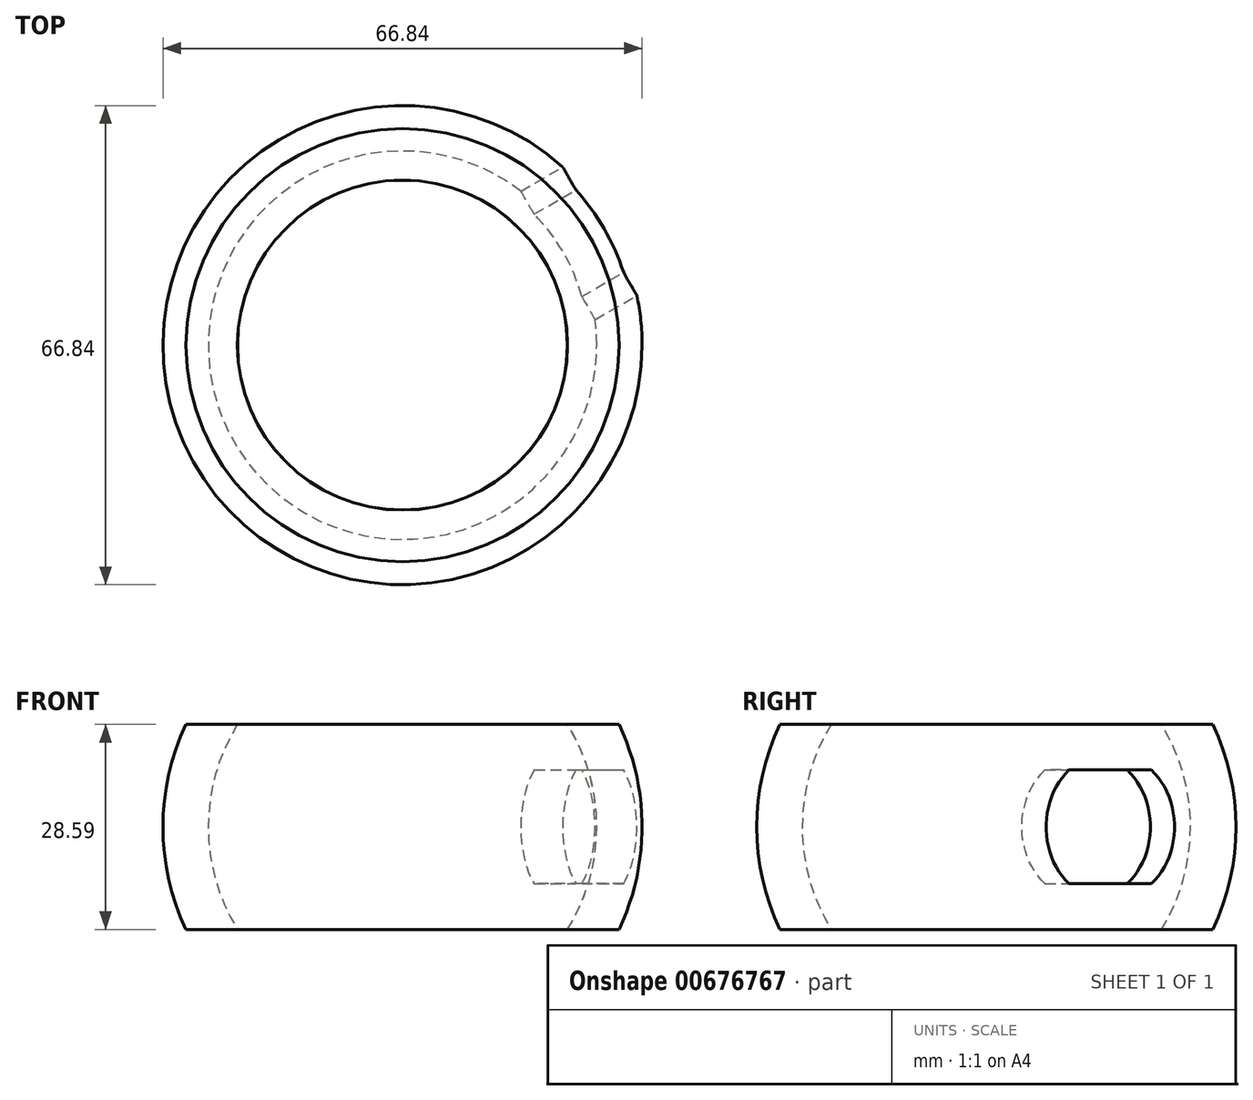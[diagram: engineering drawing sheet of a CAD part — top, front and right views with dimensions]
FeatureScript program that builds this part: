
annotation { "Feature Type Name" : "Feature", "Feature Type Description" : "" }
export const myFeature = defineFeature(function(context is Context, id is Id, definition is map)
    precondition{}
    {
        {
            var Q0;
            Q0=qCreatedBy(makeId("Front.planeOp"),FACE);
            var sketch = newSketch(context, id + "F0", { "sketchPlane" : qUnion([Q0])});
            skArc(sketch, "E0", {"start": v(-23.02, 0) * mm, "mid": v(-27.1, -14.3) * mm, "end": v(-23.01, -28.59) * mm});
            skLineSegment(sketch, "E1", {"start": v(-23.01, -28.59) * mm, "end": v(-30.2, -28.59) * mm});
            skArc(sketch, "E2", {"start": v(-30.21, 0) * mm, "mid": v(-33.42, -14.3) * mm, "end": v(-30.2, -28.59) * mm});
            skLineSegment(sketch, "E3", {"start": v(-23.02, 0) * mm, "end": v(-30.21, 0) * mm});
            skLineSegment(sketch, "E4", {"start": v(0, 0) * mm, "end": v(0, -26.06) * mm});
            skSolve(sketch);
        }
        {
            var Q0;
            Q0=makeQuery(id+"F0.imprint","IMPRINT",FACE,{"disambiguationData":[TD([[makeQuery(id+"F0.imprint","IMPRINT",EDGE,{"derivedFrom":sQuery(id+"F0.wireOp",EDGE,"E0")}),-1.0]])]});
            var Q1;
            Q1=sQuery(id+"F0.wireOp",EDGE,"E4");
            revolve(context, id + "F1", {"entities" : qUnion([Q0]), "axis" : qUnion([Q1]), "revolveType" : RevolveType.FULL});
        }
        {
            var Q0;
            Q0=makeQuery(id+"F1.opRevolve","SWEPT_FACE",FACE,{"disambiguationData":[OSD([sQuery(id+"F0.wireOp",EDGE,"E3")])]});
            var sketch = newSketch(context, id + "F2", { "sketchPlane" : qUnion([Q0])});
            skCircle(sketch, "E5", {"center": v(0, 0) * mm, "radius": 33.42 * mm});
            skLineSegment(sketch, "E6", {"start": v(0, 0) * mm, "end": v(0, 33.42) * mm});
            skLineSegment(sketch, "E7", {"start": v(0, 0) * mm, "end": v(28.94, 16.7) * mm});
            skLineSegment(sketch, "E8", {"start": v(0, 0) * mm, "end": v(-28.94, -16.7) * mm});
            skLineSegment(sketch, "E9", {"start": v(0, 0) * mm, "end": v(-28.94, 16.7) * mm});
            skSolve(sketch);
        }
        {
            var Q0;
            Q0=sQuery(id+"F2.wireOp",VERTEX,"E7.end");
            var Q1;
            Q1=sQuery(id+"F2.wireOp",EDGE,"E7");
            cPlane(context, id + "F3", {"entities" : qUnion([Q0, Q1]), "cplaneType" : CPlaneType.LINE_POINT, "offset" : 25.4 * mm, "width" : 152.4 * mm, "height" : 152.4 * mm});
        }
        {
            var Q0;
            Q0=qCreatedBy(id+"F3.planeOp",FACE);
            var sketch = newSketch(context, id + "F4", { "sketchPlane" : qUnion([Q0])});
            skLineSegment(sketch, "E10.top", {"start": v(6.64, -22.23) * mm, "end": v(-6.64, -22.23) * mm});
            skPoint(sketch, "E10.middle", {"position": v(0, -14.29) * mm});
            skPoint(sketch, "E11.visualSharp", {"position": v(11.7, -6.35) * mm});
            skLineSegment(sketch, "E11.filletArc", {"start": v(11.7, -6.35) * mm, "end": v(11.7, -6.35) * mm});
            skArc(sketch, "E12", {"start": v(-6.64, -6.35) * mm, "mid": v(-10.35, -14.29) * mm, "end": v(-6.64, -22.23) * mm});
            skLineSegment(sketch, "E13", {"start": v(-6.64, -6.35) * mm, "end": v(6.64, -6.35) * mm});
            skArc(sketch, "E14.trimOffspring", {"start": v(6.64, -22.23) * mm, "mid": v(10.35, -14.29) * mm, "end": v(6.64, -6.35) * mm});
            skPoint(sketch, "E15.orphan", {"position": v(11.7, -22.23) * mm});
            skSolve(sketch);
        }
        {
            var Q0;
            Q0 = qSketchRegion(id + "F4", true);
            extrude(context, id + "F5", {"entities" : qUnion([Q0]), "operationType" : NewBodyOperationType.REMOVE, "oppositeDirection" : true, "depth" : 12.7 * mm, "offsetDistance" : 25.4 * mm});
        }
    });
